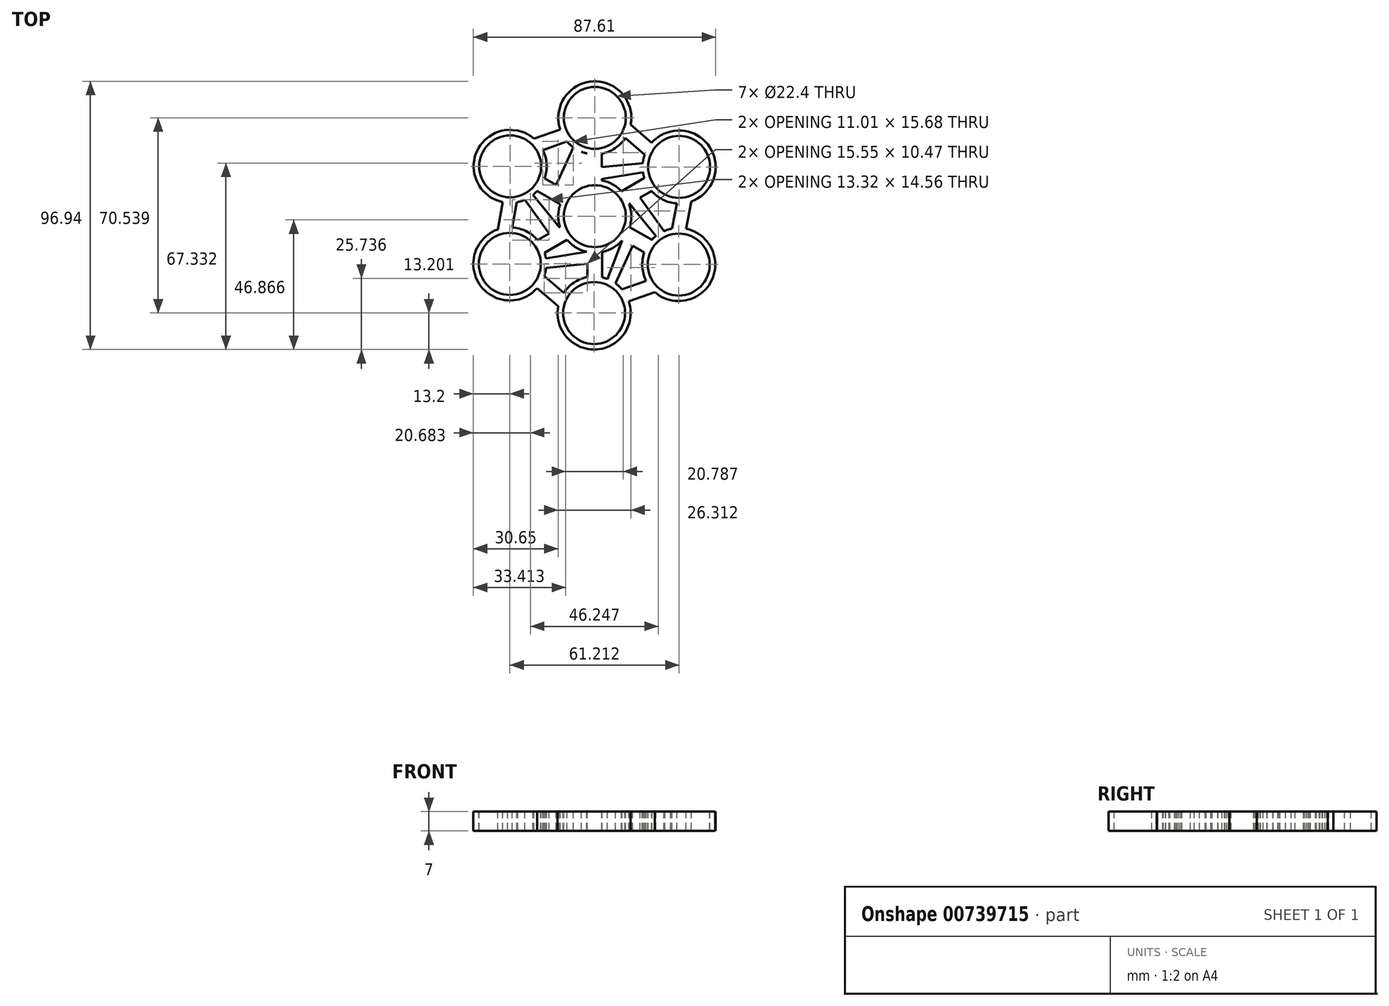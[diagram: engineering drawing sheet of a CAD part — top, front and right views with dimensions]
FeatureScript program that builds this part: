
annotation { "Feature Type Name" : "Feature", "Feature Type Description" : "" }
export const myFeature = defineFeature(function(context is Context, id is Id, definition is map)
    precondition{}
    {
        {
            var Q0;
            Q0=qCreatedBy(makeId("Top.planeOp"),FACE);
            var sketch = newSketch(context, id + "F0", { "sketchPlane" : qUnion([Q0])});
            skCircle(sketch, "E0", {"center": v(0, 0) * mm, "radius": 11.2 * mm});
            skArc(sketch, "E1", {"start": v(-2.84, 12.89) * mm, "mid": v(0.18, -13.2) * mm, "end": v(2.5, 12.96) * mm});
            skCircle(sketch, "E2", {"center": v(0, 35.54) * mm, "radius": 11.2 * mm});
            skArc(sketch, "E3", {"start": v(12.97, 33.09) * mm, "mid": v(3.12, 48.37) * mm, "end": v(-12.65, 39.32) * mm});
            skCircle(sketch, "E4.1.0", {"center": v(-30.6, 18.01) * mm, "radius": 11.2 * mm});
            skArc(sketch, "E4.1.1", {"start": v(-22, 28.02) * mm, "mid": v(-24.73, 29.83) * mm, "end": v(-27.82, 30.91) * mm});
            skCircle(sketch, "E4.2.0", {"center": v(-30.73, -17.26) * mm, "radius": 11.2 * mm});
            skArc(sketch, "E4.2.1", {"start": v(-20.75, -8.61) * mm, "mid": v(-24.87, -5.43) * mm, "end": v(-29.9, -4.08) * mm});
            skCircle(sketch, "E4.3.0", {"center": v(-0.25, -35) * mm, "radius": 11.2 * mm});
            skArc(sketch, "E4.3.1", {"start": v(-2.74, -22.04) * mm, "mid": v(-6.91, -46.4) * mm, "end": v(12.28, -30.82) * mm});
            skCircle(sketch, "E4.4.0", {"center": v(30.36, -17.47) * mm, "radius": 11.2 * mm});
            skArc(sketch, "E4.4.1", {"start": v(27.96, -4.5) * mm, "mid": v(26.46, -4.86) * mm, "end": v(25, -5.4) * mm});
            skCircle(sketch, "E4.5.0", {"center": v(30.48, 17.8) * mm, "radius": 11.2 * mm});
            skArc(sketch, "E4.5.1", {"start": v(17.43, 15.83) * mm, "mid": v(17.62, 14.82) * mm, "end": v(17.9, 13.82) * mm});
            skPoint(sketch, "E4.center", {"position": v(-0.12, 0.27) * mm});
            skLineSegment(sketch, "E5", {"start": v(12.97, 33.09) * mm, "end": v(20.6, 26.56) * mm});
            skLineSegment(sketch, "E6", {"start": v(18.04, 22.21) * mm, "end": v(11, 28.24) * mm});
            skLineSegment(sketch, "E7.1.0", {"start": v(-22, 28.02) * mm, "end": v(-12.52, 31.36) * mm});
            skLineSegment(sketch, "E7.1.1", {"start": v(-10.04, 26.97) * mm, "end": v(-18.78, 23.89) * mm});
            skLineSegment(sketch, "E7.2.0", {"start": v(-35.09, -4.8) * mm, "end": v(-33.25, 5.08) * mm});
            skLineSegment(sketch, "E7.2.1", {"start": v(-28.2, 5.03) * mm, "end": v(-29.9, -4.08) * mm});
            skLineSegment(sketch, "E7.3.0", {"start": v(-13.22, -32.55) * mm, "end": v(-20.85, -26.01) * mm});
            skLineSegment(sketch, "E7.3.1", {"start": v(-18.29, -21.67) * mm, "end": v(-11.24, -27.7) * mm});
            skLineSegment(sketch, "E7.4.0", {"start": v(21.75, -27.48) * mm, "end": v(12.28, -30.82) * mm});
            skLineSegment(sketch, "E7.4.1", {"start": v(9.8, -26.43) * mm, "end": v(18.54, -23.34) * mm});
            skLineSegment(sketch, "E7.5.0", {"start": v(34.84, 5.34) * mm, "end": v(33, -4.54) * mm});
            skLineSegment(sketch, "E7.5.1", {"start": v(27.96, -4.5) * mm, "end": v(29.66, 4.62) * mm});
            skPoint(sketch, "E8.start.orphan", {"position": v(0, 22.34) * mm});
            skLineSegment(sketch, "E9", {"start": v(-2.84, 12.89) * mm, "end": v(-2.84, 22.65) * mm});
            skLineSegment(sketch, "E10", {"start": v(2.5, 12.96) * mm, "end": v(2.5, 13.4) * mm});
            skLineSegment(sketch, "E11.1.0", {"start": v(-9.8, 8.89) * mm, "end": v(-10.18, 9.1) * mm});
            skLineSegment(sketch, "E11.1.1", {"start": v(-12.41, 4.22) * mm, "end": v(-20.87, 9.1) * mm});
            skArc(sketch, "E11.1.2", {"start": v(0, 22.34) * mm, "mid": v(10.58, 43.43) * mm, "end": v(-12.65, 39.32) * mm});
            skLineSegment(sketch, "E11.2.0", {"start": v(-12.42, -3.8) * mm, "end": v(-12.8, -4.02) * mm});
            skLineSegment(sketch, "E11.2.1", {"start": v(-9.7, -8.4) * mm, "end": v(-18.14, -13.28) * mm});
            skLineSegment(sketch, "E12.1.3.0", {"start": v(-2.74, -12.42) * mm, "end": v(-2.74, -12.86) * mm});
            skLineSegment(sketch, "E12.3.3.0", {"start": v(2.6, -12.35) * mm, "end": v(2.6, -22.1) * mm});
            skArc(sketch, "E12.6.3.0", {"start": v(-35.09, -4.8) * mm, "mid": v(-41.7, -24.61) * mm, "end": v(-20.85, -26.01) * mm});
            skLineSegment(sketch, "E12.1.4.0", {"start": v(9.56, -8.34) * mm, "end": v(9.94, -8.56) * mm});
            skLineSegment(sketch, "E12.3.4.0", {"start": v(12.17, -3.68) * mm, "end": v(20.62, -8.56) * mm});
            skArc(sketch, "E12.6.4.0", {"start": v(-13.22, -32.55) * mm, "mid": v(0.64, -48.17) * mm, "end": v(12.28, -30.82) * mm});
            skLineSegment(sketch, "E12.1.5.0", {"start": v(12.18, 4.35) * mm, "end": v(12.56, 4.56) * mm});
            skLineSegment(sketch, "E12.3.5.0", {"start": v(9.44, 8.94) * mm, "end": v(17.9, 13.82) * mm});
            skArc(sketch, "E12.6.5.0", {"start": v(22.13, -7.15) * mm, "mid": v(21.35, -7.83) * mm, "end": v(20.62, -8.56) * mm});
            skPoint(sketch, "E13.end.orphan", {"position": v(13.67, 11.38) * mm});
            skLineSegment(sketch, "E14", {"start": v(-13.97, 11.29) * mm, "end": v(-7.77, 24.87) * mm});
            skLineSegment(sketch, "E15.1.0", {"start": v(-12.8, -4.02) * mm, "end": v(-22.38, 7.7) * mm});
            skLineSegment(sketch, "E15.1.1", {"start": v(-16.59, -6.2) * mm, "end": v(-25.26, 5.95) * mm});
            skLineSegment(sketch, "E15.2.0", {"start": v(-2.74, -12.86) * mm, "end": v(-17.68, -15.3) * mm});
            skLineSegment(sketch, "E15.2.1", {"start": v(-2.74, -17.23) * mm, "end": v(-17.6, -18.66) * mm});
            skLineSegment(sketch, "E15.3.0", {"start": v(9.94, -8.56) * mm, "end": v(4.58, -22.71) * mm});
            skLineSegment(sketch, "E15.3.1", {"start": v(13.72, -10.75) * mm, "end": v(7.53, -24.33) * mm});
            skLineSegment(sketch, "E15.4.0", {"start": v(12.56, 4.56) * mm, "end": v(22.13, -7.15) * mm});
            skLineSegment(sketch, "E15.4.1", {"start": v(16.34, 6.75) * mm, "end": v(25, -5.4) * mm});
            skLineSegment(sketch, "E15.5.0", {"start": v(2.5, 13.4) * mm, "end": v(17.43, 15.83) * mm});
            skLineSegment(sketch, "E15.5.1", {"start": v(2.5, 17.77) * mm, "end": v(17.36, 19.2) * mm});
            skLineSegment(sketch, "E16.trimOffspring", {"start": v(2.5, 17.77) * mm, "end": v(2.5, 22.58) * mm});
            skArc(sketch, "E17.trimOffspring", {"start": v(20.5, 9.15) * mm, "mid": v(24.63, 5.97) * mm, "end": v(29.66, 4.62) * mm});
            skArc(sketch, "E18.trimOffspring", {"start": v(18.04, 22.21) * mm, "mid": v(17.61, 20.73) * mm, "end": v(17.36, 19.2) * mm});
            skArc(sketch, "E19.trimOffspring", {"start": v(2.5, 22.58) * mm, "mid": v(7.32, 24.55) * mm, "end": v(11, 28.24) * mm});
            skArc(sketch, "E20.trimOffspring", {"start": v(-4.82, 23.25) * mm, "mid": v(-3.85, 22.91) * mm, "end": v(-2.84, 22.65) * mm});
            skArc(sketch, "E21.trimOffspring", {"start": v(-10.04, 26.97) * mm, "mid": v(-8.97, 25.86) * mm, "end": v(-7.77, 24.87) * mm});
            skArc(sketch, "E22.trimOffspring", {"start": v(-18.13, 13.7) * mm, "mid": v(-17.43, 18.86) * mm, "end": v(-18.78, 23.89) * mm});
            skArc(sketch, "E23.trimOffspring", {"start": v(-22.38, 7.7) * mm, "mid": v(-21.6, 8.37) * mm, "end": v(-20.87, 9.1) * mm});
            skArc(sketch, "E24.trimOffspring", {"start": v(-28.2, 5.03) * mm, "mid": v(-26.7, 5.4) * mm, "end": v(-25.26, 5.95) * mm});
            skArc(sketch, "E25.trimOffspring", {"start": v(-35.09, -4.8) * mm, "mid": v(-43.4, -20.97) * mm, "end": v(-27.68, -30.1) * mm});
            skArc(sketch, "E26.trimOffspring", {"start": v(-17.68, -15.3) * mm, "mid": v(-17.87, -14.27) * mm, "end": v(-18.14, -13.28) * mm});
            skArc(sketch, "E27.trimOffspring", {"start": v(-18.29, -21.67) * mm, "mid": v(-17.86, -20.18) * mm, "end": v(-17.6, -18.66) * mm});
            skArc(sketch, "E28.trimOffspring", {"start": v(-2.74, -22.04) * mm, "mid": v(-7.56, -24.01) * mm, "end": v(-11.24, -27.7) * mm});
            skArc(sketch, "E29.trimOffspring", {"start": v(4.58, -22.71) * mm, "mid": v(3.6, -22.37) * mm, "end": v(2.6, -22.1) * mm});
            skArc(sketch, "E30.trimOffspring", {"start": v(9.8, -26.43) * mm, "mid": v(8.72, -25.32) * mm, "end": v(7.53, -24.33) * mm});
            skArc(sketch, "E31.trimOffspring", {"start": v(34.84, 5.34) * mm, "mid": v(41.44, 25.15) * mm, "end": v(20.6, 26.56) * mm});
            skArc(sketch, "E32.trimOffspring", {"start": v(17.89, -13.15) * mm, "mid": v(17.19, -18.31) * mm, "end": v(18.54, -23.34) * mm});
            skArc(sketch, "E33.trimOffspring", {"start": v(17.89, -13.15) * mm, "mid": v(40.08, -26.4) * mm, "end": v(25, -5.4) * mm});
            skArc(sketch, "E34.trimOffspring", {"start": v(21.75, -27.48) * mm, "mid": v(42.2, -23.29) * mm, "end": v(33, -4.54) * mm});
            skLineSegment(sketch, "E35.trimOffspring", {"start": v(-13.97, 11.29) * mm, "end": v(-18.13, 13.7) * mm});
            skLineSegment(sketch, "E36.trimOffspring", {"start": v(-2.74, -17.23) * mm, "end": v(-2.74, -22.04) * mm});
            skLineSegment(sketch, "E37.trimOffspring", {"start": v(-16.59, -6.2) * mm, "end": v(-20.75, -8.61) * mm});
            skLineSegment(sketch, "E38.trimOffspring", {"start": v(13.72, -10.75) * mm, "end": v(17.89, -13.15) * mm});
            skLineSegment(sketch, "E39.trimOffspring", {"start": v(16.34, 6.75) * mm, "end": v(20.5, 9.15) * mm});
            skLineSegment(sketch, "E40", {"start": v(12.57, 39.58) * mm, "end": v(25.34, 29.96) * mm});
            skLineSegment(sketch, "E41", {"start": v(25.34, 29.96) * mm, "end": v(27.43, 30.64) * mm});
            skPoint(sketch, "E42.end.orphan", {"position": v(12.57, 42.87) * mm});
            skLineSegment(sketch, "E43", {"start": v(27.43, 30.64) * mm, "end": v(10.97, 42.87) * mm});
            skLineSegment(sketch, "E44.2.0", {"start": v(-40.5, -8.4) * mm, "end": v(-38.57, 7.48) * mm});
            skLineSegment(sketch, "E44.2.1", {"start": v(-40.2, 8.95) * mm, "end": v(-42.57, -11.42) * mm});
            skLineSegment(sketch, "E44.3.0", {"start": v(-12.82, -39.04) * mm, "end": v(-25.59, -29.42) * mm});
            skLineSegment(sketch, "E44.3.1", {"start": v(-27.68, -30.1) * mm, "end": v(-11.22, -42.33) * mm});
            skLineSegment(sketch, "E44.4.0", {"start": v(27.57, -30.37) * mm, "end": v(12.85, -36.63) * mm});
            skLineSegment(sketch, "E44.4.1", {"start": v(12.4, -38.77) * mm, "end": v(31.22, -30.64) * mm});
            skLineSegment(sketch, "E44.5.0", {"start": v(40.26, 8.93) * mm, "end": v(38.32, -6.94) * mm});
            skLineSegment(sketch, "E44.5.1", {"start": v(39.95, -8.4) * mm, "end": v(42.32, 11.96) * mm});
            skArc(sketch, "E45.trimOffspring", {"start": v(-13.1, 37.17) * mm, "mid": v(-13.14, 34.23) * mm, "end": v(-12.52, 31.36) * mm});
            skArc(sketch, "E46.trimOffspring", {"start": v(-31.47, 31.18) * mm, "mid": v(-43.78, 18.91) * mm, "end": v(-33.25, 5.08) * mm});
            skArc(sketch, "E47.trimOffspring", {"start": v(-25.59, -29.42) * mm, "mid": v(-23.03, -27.98) * mm, "end": v(-20.85, -26.01) * mm});
            skLineSegment(sketch, "E48", {"start": v(-31.47, 31.18) * mm, "end": v(-27.82, 30.91) * mm});
            skLineSegment(sketch, "E49", {"start": v(-27.82, 30.91) * mm, "end": v(-31.47, 31.18) * mm});
            skLineSegment(sketch, "E50", {"start": v(-12.65, 39.32) * mm, "end": v(-13.1, 37.17) * mm});
            skLineSegment(sketch, "E51", {"start": v(-4.82, 23.25) * mm, "end": v(-2.84, 22.65) * mm});
            skLineSegment(sketch, "E52", {"start": v(-2.84, 22.65) * mm, "end": v(-4.82, 23.25) * mm});
            skLineSegment(sketch, "E53", {"start": v(-10.18, 9.1) * mm, "end": v(-4.82, 23.25) * mm});
            skLineSegment(sketch, "E54", {"start": v(-7.77, 24.87) * mm, "end": v(-4.82, 23.25) * mm});
            skSolve(sketch);
        }
        {
            var Q0;
            Q0=makeQuery(id+"F0.imprint","IMPRINT",FACE,{"disambiguationData":[TD([[makeQuery(id+"F0.imprint","IMPRINT",EDGE,{"derivedFrom":sQuery(id+"F0.wireOp",EDGE,"E0")}),-1.0]])]});
            extrude(context, id + "F1", {"entities" : qUnion([Q0]), "oppositeDirection" : true, "depth" : 7 * mm, "offsetDistance" : 25 * mm});
        }
    });
